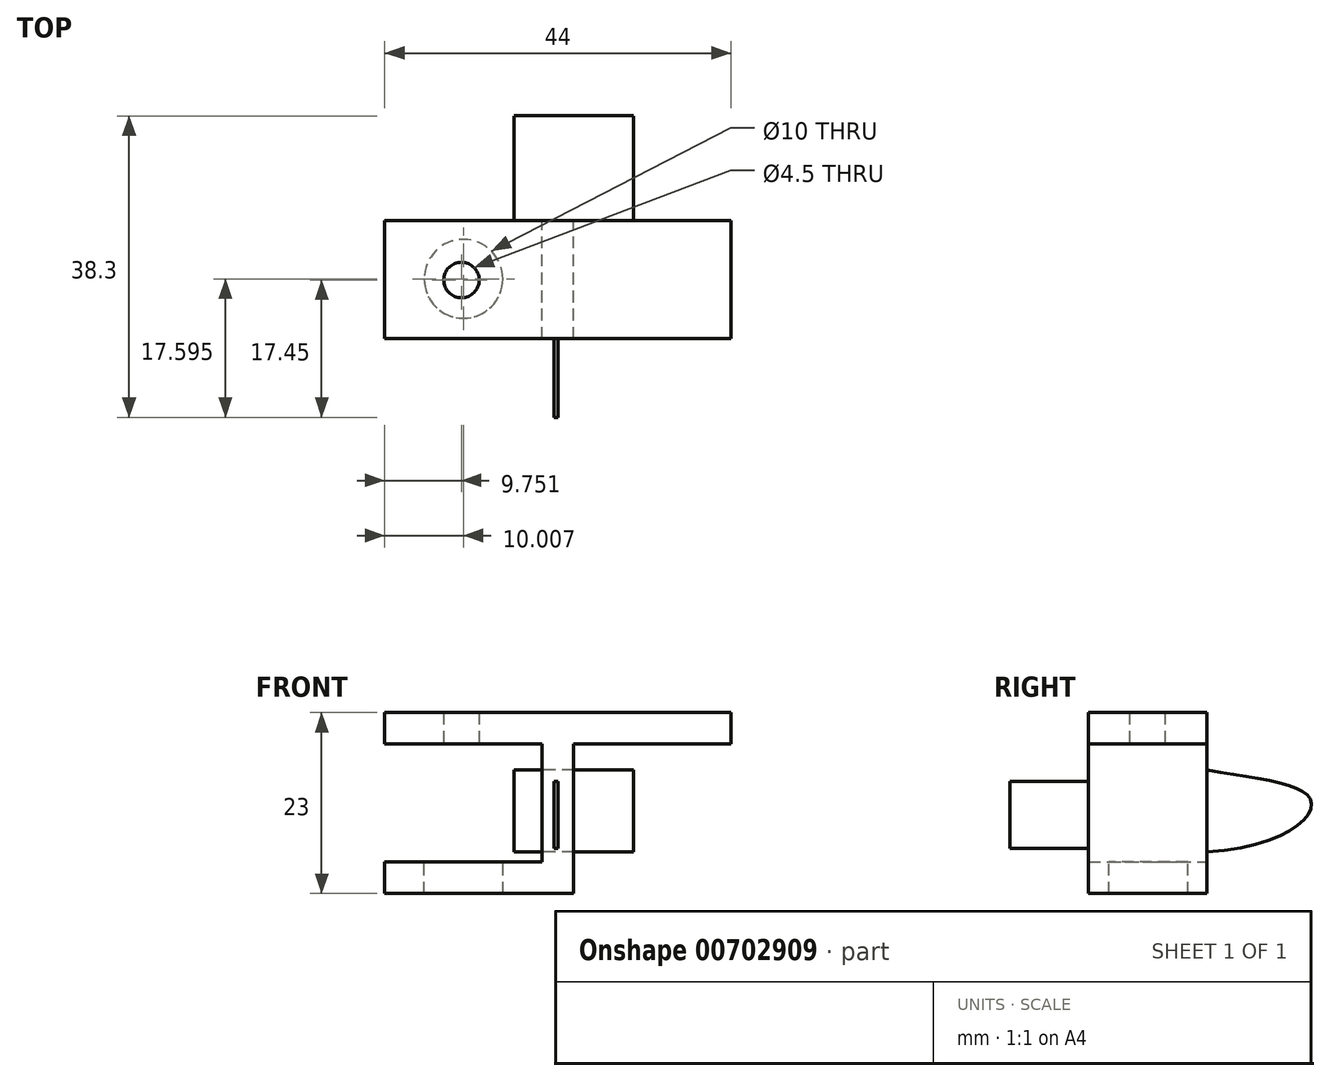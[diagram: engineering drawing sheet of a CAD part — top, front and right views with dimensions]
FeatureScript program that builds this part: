
annotation { "Feature Type Name" : "Feature", "Feature Type Description" : "" }
export const myFeature = defineFeature(function(context is Context, id is Id, definition is map)
    precondition{}
    {
        {
            var Q0;
            Q0=qCreatedBy(makeId("Front.planeOp"),FACE);
            var sketch = newSketch(context, id + "F0", { "sketchPlane" : qUnion([Q0])});
            skPoint(sketch, "E0.middle", {"position": v(0, 0) * mm});
            skLineSegment(sketch, "E1.bottom", {"start": v(24, 4) * mm, "end": v(20, 4) * mm});
            skLineSegment(sketch, "E1.top", {"start": v(24, 19) * mm, "end": v(20, 19) * mm});
            skLineSegment(sketch, "E1.left", {"start": v(24, 4) * mm, "end": v(24, 19) * mm});
            skLineSegment(sketch, "E1.right", {"start": v(20, 4) * mm, "end": v(20, 19) * mm});
            skLineSegment(sketch, "E2.top", {"start": v(0, 23) * mm, "end": v(44, 23) * mm});
            skLineSegment(sketch, "E2.left", {"start": v(0, 19) * mm, "end": v(0, 23) * mm});
            skLineSegment(sketch, "E2.right", {"start": v(44, 19) * mm, "end": v(44, 23) * mm});
            skLineSegment(sketch, "E3.bottom", {"start": v(24, 4) * mm, "end": v(0, 4) * mm});
            skLineSegment(sketch, "E3.top", {"start": v(24, 0) * mm, "end": v(0, 0) * mm});
            skLineSegment(sketch, "E3.left", {"start": v(24, 4) * mm, "end": v(24, 0) * mm});
            skLineSegment(sketch, "E3.right", {"start": v(0, 4) * mm, "end": v(0, 0) * mm});
            skLineSegment(sketch, "E4", {"start": v(0, 19) * mm, "end": v(44, 19) * mm});
            skSolve(sketch);
        }
        {
            var Q0;
            Q0=makeQuery(id+"F0.imprint","IMPRINT",FACE,{"disambiguationData":[TD([[makeQuery(id+"F0.imprint","IMPRINT",EDGE,{"derivedFrom":sQuery(id+"F0.wireOp",EDGE,"E3.top")}),-1.0]])]});
            var Q1;
            {var subQ0=sQuery(id+"F0.wireOp",EDGE,"E1.left");Q1=makeQuery(id+"F0.imprint","IMPRINT",FACE,{"disambiguationData":[TD([[makeQuery(id+"F0.imprint","IMPRINT",EDGE,{"derivedFrom":subQ0}),1.0]])]});}
            var Q2;
            Q2=makeQuery(id+"F0.imprint","IMPRINT",FACE,{"disambiguationData":[TD([[makeQuery(id+"F0.imprint","IMPRINT",EDGE,{"derivedFrom":sQuery(id+"F0.wireOp",EDGE,"E2.top")}),-1.0]])]});
            extrude(context, id + "F1", {"entities" : qUnion([Q0, Q1, Q2]), "depth" : 15 * mm, "offsetDistance" : 25 * mm});
        }
        {
            var Q0;
            Q0=makeQuery(id+"F1.opExtrude","SWEPT_FACE",FACE,{"disambiguationData":[OSD([sQuery(id+"F0.wireOp",EDGE,"E3.bottom")])]});
            var sketch = newSketch(context, id + "F2", { "sketchPlane" : qUnion([Q0])});
            skCircle(sketch, "E5", {"center": v(10, -7.4) * mm, "radius": 5 * mm});
            skSolve(sketch);
        }
        {
            var Q0;
            Q0 = qSketchRegion(id + "F2", true);
            extrude(context, id + "F3", {"entities" : qUnion([Q0]), "operationType" : NewBodyOperationType.REMOVE, "endBound" : BoundingType.THROUGH_ALL, "oppositeDirection" : true, "depth" : 25 * mm, "offsetDistance" : 25 * mm});
        }
        {
            var Q0;
            {var subQ0=sQuery(id+"F0.wireOp",EDGE,"E4");Q0=makeQuery(id+"F1.opExtrude","SWEPT_FACE",FACE,{"disambiguationData":[OSD([subQ0]),TDD([makeQuery(id+"F0.imprint","IMPRINT",EDGE,{"disambiguationData":[TD([[makeQuery(id+"F0.imprint","INTERSECT",VERTEX,{"derivedFrom":[sQuery(id+"F0.wireOp",EDGE,"E1.right"),subQ0]}),1.0]])],"derivedFrom":subQ0})])]});}
            var sketch = newSketch(context, id + "F4", { "sketchPlane" : qUnion([Q0])});
            skCircle(sketch, "E6", {"center": v(9.75, 7.55) * mm, "radius": 2.25 * mm});
            skSolve(sketch);
        }
        {
            var Q0;
            Q0 = qSketchRegion(id + "F4", true);
            extrude(context, id + "F5", {"entities" : qUnion([Q0]), "operationType" : NewBodyOperationType.REMOVE, "endBound" : BoundingType.THROUGH_ALL, "oppositeDirection" : true, "depth" : 25 * mm, "offsetDistance" : 25 * mm});
        }
        {
            var Q0;
            Q0=makeQuery(id+"F1.opExtrude","CAP_FACE",FACE,{"disambiguationData":[OSD([sQuery(id+"F0.wireOp",EDGE,"E1.left"),sQuery(id+"F0.wireOp",EDGE,"E1.right"),sQuery(id+"F0.wireOp",EDGE,"E2.top"),sQuery(id+"F0.wireOp",EDGE,"E2.left"),sQuery(id+"F0.wireOp",EDGE,"E2.right"),sQuery(id+"F0.wireOp",EDGE,"E3.bottom"),sQuery(id+"F0.wireOp",EDGE,"E3.top"),sQuery(id+"F0.wireOp",EDGE,"E3.left"),sQuery(id+"F0.wireOp",EDGE,"E3.right"),sQuery(id+"F0.wireOp",EDGE,"E4")])],"isStart":false});
            var sketch = newSketch(context, id + "F6", { "sketchPlane" : qUnion([Q0])});
            skLineSegment(sketch, "E7.bottom", {"start": v(21.5, 14.27) * mm, "end": v(22, 14.27) * mm});
            skLineSegment(sketch, "E7.top", {"start": v(21.5, 5.77) * mm, "end": v(22, 5.77) * mm});
            skLineSegment(sketch, "E7.left", {"start": v(21.5, 14.27) * mm, "end": v(21.5, 5.77) * mm});
            skLineSegment(sketch, "E7.right", {"start": v(22, 14.27) * mm, "end": v(22, 5.77) * mm});
            skSolve(sketch);
        }
        {
            var Q0;
            Q0 = qSketchRegion(id + "F6", true);
            extrude(context, id + "F7", {"entities" : qUnion([Q0]), "operationType" : NewBodyOperationType.ADD, "depth" : 10 * mm, "offsetDistance" : 25 * mm});
        }
        {
            var Q0;
            Q0=makeQuery(id+"F1.opExtrude","SWEPT_FACE",FACE,{"disambiguationData":[OSD([sQuery(id+"F0.wireOp",EDGE,"E1.left"),sQuery(id+"F0.wireOp",EDGE,"E3.left")])]});
            var sketch = newSketch(context, id + "F8", { "sketchPlane" : qUnion([Q0])});
            skFitSpline(sketch, "E8", {"points": [v(0, 15.7) * mm, v(13.23, 11.84) * mm, v(0, 5.32) * mm], "startDerivative": vector(39.91, -6.63) * mm, "endDerivative": vector(-54.17, -2.43) * mm});
            skLineSegment(sketch, "E9", {"start": v(0, 15.7) * mm, "end": v(0, 5.32) * mm});
            skSolve(sketch);
        }
        {
            var Q0;
            Q0=makeQuery(id+"F8.imprint","IMPRINT",FACE,{"disambiguationData":[TD([[makeQuery(id+"F8.imprint","IMPRINT",EDGE,{"derivedFrom":sQuery(id+"F8.wireOp",EDGE,"E8")}),-1.0]])]});
            extrude(context, id + "F9", {"entities" : qUnion([Q0]), "operationType" : NewBodyOperationType.ADD, "endBound" : BoundingType.SYMMETRIC, "depth" : 15.2 * mm, "offsetDistance" : 25 * mm});
        }
    });
